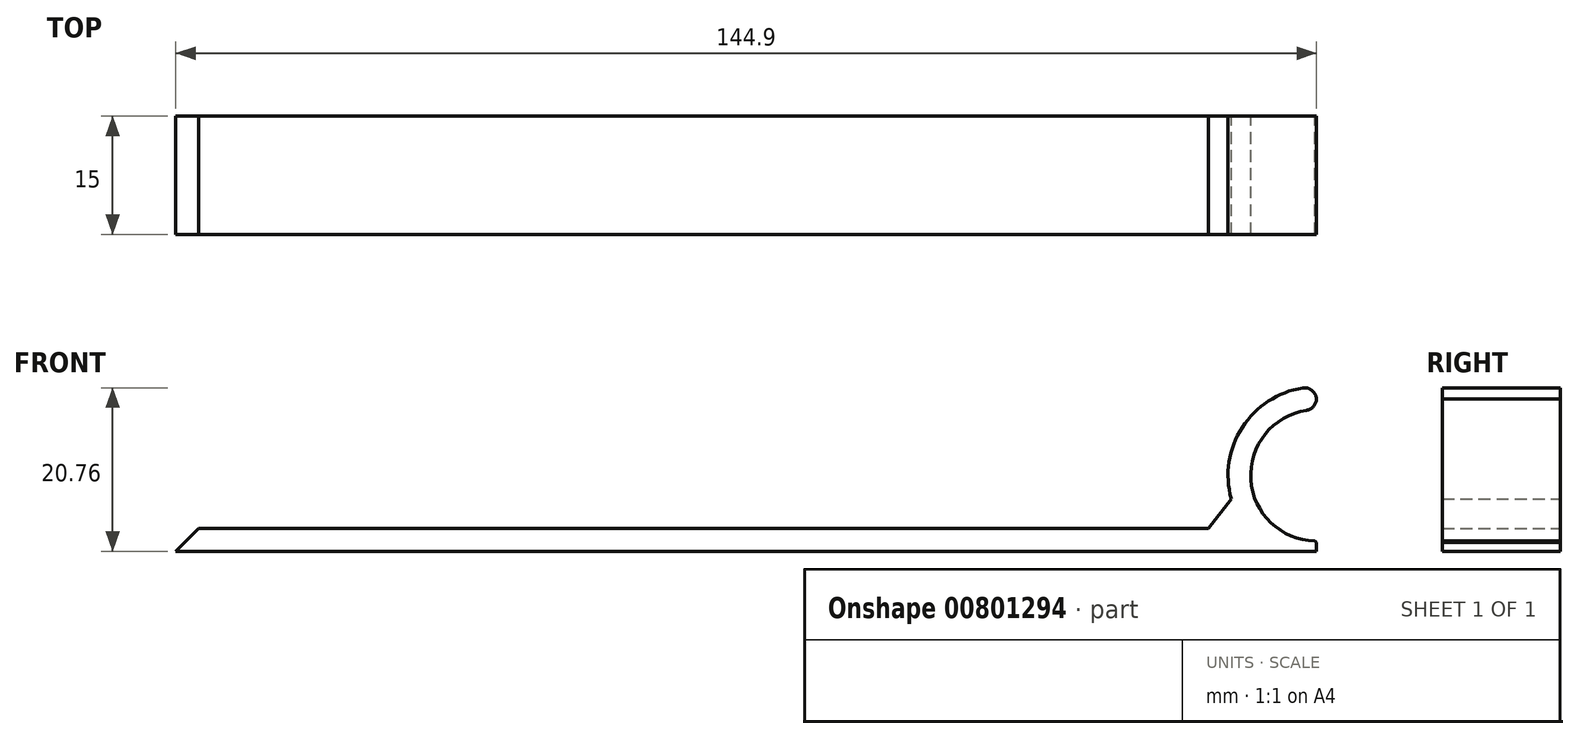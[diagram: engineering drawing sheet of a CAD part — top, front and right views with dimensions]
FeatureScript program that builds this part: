
annotation { "Feature Type Name" : "Feature", "Feature Type Description" : "" }
export const myFeature = defineFeature(function(context is Context, id is Id, definition is map)
    precondition{}
    {
        {
            var Q0;
            Q0=qCreatedBy(makeId("Front.planeOp"),FACE);
            var sketch = newSketch(context, id + "F0", { "sketchPlane" : qUnion([Q0])});
            skLineSegment(sketch, "E0.bottom", {"start": v(72.5, 1.58) * mm, "end": v(62.54, 1.58) * mm});
            skLineSegment(sketch, "E0.top", {"start": v(72.5, -1.58) * mm, "end": v(-72.5, -1.58) * mm});
            skLineSegment(sketch, "E0.left", {"start": v(72.5, 1.58) * mm, "end": v(72.5, -1.58) * mm});
            skLineSegment(sketch, "E0.right", {"start": v(-72.5, 0) * mm, "end": v(-72.5, -1.58) * mm});
            skPoint(sketch, "E0.middle", {"position": v(0, 0) * mm});
            skLineSegment(sketch, "E1", {"start": v(72.5, -1.58) * mm, "end": v(72.5, 6.77) * mm, "construction": true});
            skCircle(sketch, "E2", {"center": v(72.5, 6.77) * mm, "radius": 8.35 * mm});
            skCircle(sketch, "E3", {"center": v(72.5, 6.77) * mm, "radius": 11.23 * mm});
            skLineSegment(sketch, "E4", {"start": v(72.5, 15.12) * mm, "end": v(72.5, 18) * mm});
            skLineSegment(sketch, "E5.bottom", {"start": v(-72.5, -1.58) * mm, "end": v(72.5, -1.58) * mm});
            skLineSegment(sketch, "E5.top", {"start": v(-72.5, -2.88) * mm, "end": v(72.5, -2.88) * mm});
            skLineSegment(sketch, "E5.left", {"start": v(-72.5, -1.58) * mm, "end": v(-72.5, -2.88) * mm});
            skLineSegment(sketch, "E5.right", {"start": v(72.5, -1.58) * mm, "end": v(72.5, -2.88) * mm});
            skLineSegment(sketch, "E6.top", {"start": v(-72.5, 0) * mm, "end": v(72.5, 0) * mm});
            skLineSegment(sketch, "E6.left", {"start": v(-72.5, -1.58) * mm, "end": v(-72.5, 0) * mm});
            skLineSegment(sketch, "E6.right", {"start": v(72.5, -1.58) * mm, "end": v(72.5, 0) * mm});
            skPoint(sketch, "E7.orphan", {"position": v(-72.5, 1.58) * mm});
            skSolve(sketch);
        }
        {
            var Q0;
            {var subQ0=sQuery(id+"F0.wireOp",EDGE,"E0.right");Q0=makeQuery(id+"F0.imprint","IMPRINT",FACE,{"disambiguationData":[TD([[makeQuery(id+"F0.imprint","IMPRINT",EDGE,{"derivedFrom":subQ0}),1.0]])]});}
            var Q1;
            {var subQ0=sQuery(id+"F0.wireOp",EDGE,"E0.left");var subQ1=sQuery(id+"F0.wireOp",EDGE,"E0.top");var subQ2=makeQuery(id+"F0.imprint","INTERSECT",VERTEX,{"derivedFrom":[subQ1,subQ0]});Q1=makeQuery(id+"F0.imprint","IMPRINT",FACE,{"disambiguationData":[TD([[makeQuery(id+"F0.imprint","IMPRINT",EDGE,{"disambiguationData":[TD([[subQ2,-1.0]])],"derivedFrom":subQ1}),-1.0]])]});}
            var Q2;
            {var subQ5=sQuery(id+"F0.wireOp",EDGE,"urySj7C3-RO8u-xJS9-4BbJ-Gt5VhAMPYNj5");Q2=makeQuery(id+"F0.imprint","IMPRINT",FACE,{"disambiguationData":[TD([[makeQuery(id+"F0.imprint","IMPRINT",EDGE,{"derivedFrom":subQ5}),1.0]])]});}
            var Q3;
            {var subQ5=sQuery(id+"F0.wireOp",EDGE,"E4");Q3=makeQuery(id+"F0.imprint","IMPRINT",FACE,{"disambiguationData":[TD([[makeQuery(id+"F0.imprint","IMPRINT",EDGE,{"derivedFrom":subQ5}),1.0]])]});}
            var Q4;
            {var subQ5=sQuery(id+"F0.wireOp",EDGE,"E5.left");Q4=makeQuery(id+"F0.imprint","IMPRINT",FACE,{"disambiguationData":[TD([[makeQuery(id+"F0.imprint","IMPRINT",EDGE,{"derivedFrom":subQ5}),1.0]])]});}
            var Q5;
            {var subQ0=sQuery(id+"F0.wireOp",EDGE,"E3");var subQ1=sQuery(id+"F0.wireOp",EDGE,"E0.bottom");var subQ2=makeQuery(id+"F0.imprint","INTERSECT",VERTEX,{"derivedFrom":[subQ1,subQ0]});Q5=makeQuery(id+"F0.imprint","IMPRINT",FACE,{"disambiguationData":[TD([[makeQuery(id+"F0.imprint","IMPRINT",EDGE,{"disambiguationData":[TD([[subQ2,1.0]])],"derivedFrom":subQ1}),1.0]])]});}
            var Q6;
            {var subQ5=sQuery(id+"F0.wireOp",EDGE,"E5.right");Q6=makeQuery(id+"F0.imprint","IMPRINT",FACE,{"disambiguationData":[TD([[makeQuery(id+"F0.imprint","IMPRINT",EDGE,{"derivedFrom":subQ5}),-1.0]])]});}
            var Q7;
            {var subQ3=sQuery(id+"F0.wireOp",EDGE,"E6.top");var subQ5=sQuery(id+"F0.wireOp",EDGE,"E3");var subQ6=makeQuery(id+"F0.imprint","INTERSECT",VERTEX,{"derivedFrom":[subQ5,subQ3]});Q7=makeQuery(id+"F0.imprint","IMPRINT",FACE,{"disambiguationData":[TD([[makeQuery(id+"F0.imprint","IMPRINT",EDGE,{"disambiguationData":[TD([[subQ6,-1.0]])],"derivedFrom":subQ5}),1.0]])]});}
            var Q8;
            {var subQ5=sQuery(id+"F0.wireOp",EDGE,"E6.left");Q8=makeQuery(id+"F0.imprint","IMPRINT",FACE,{"disambiguationData":[TD([[makeQuery(id+"F0.imprint","IMPRINT",EDGE,{"derivedFrom":subQ5}),-1.0]])]});}
            extrude(context, id + "F1", {"entities" : qUnion([Q0, Q1, Q2, Q3, Q4, Q5, Q6, Q7, Q8]), "depth" : 15 * mm, "offsetDistance" : 25 * mm});
        }
        {
            var Q0;
            Q0=makeQuery(id+"F1.opExtrude","SWEPT_EDGE",EDGE,{"disambiguationData":[OSD([sQuery(id+"F0.wireOp",EDGE,"E0.top"),sQuery(id+"F0.wireOp",EDGE,"E0.left"),sQuery(id+"F0.wireOp",EDGE,"E2")])]});
            var Q1;
            Q1=makeQuery(id+"F1.opExtrude","SWEPT_EDGE",EDGE,{"disambiguationData":[OSD([sQuery(id+"F0.wireOp",EDGE,"E2"),sQuery(id+"F0.wireOp",EDGE,"E5.right"),sQuery(id+"F0.wireOp",EDGE,"E5.bottom"),sQuery(id+"F0.wireOp",EDGE,"E6.right")])]});
            chamfer(context, id + "F2", {"entities" : qUnion([Q0, Q1]), "width" : 0.2 * mm, "tangentPropagation" : true});
        }
        {
            var Q0;
            Q0=makeQuery(id+"F1.opExtrude","SWEPT_EDGE",EDGE,{"disambiguationData":[OSD([sQuery(id+"F0.wireOp",EDGE,"E0.bottom"),sQuery(id+"F0.wireOp",EDGE,"E0.right")])]});
            var Q1;
            Q1=makeQuery(id+"F1.opExtrude","SWEPT_EDGE",EDGE,{"disambiguationData":[OSD([sQuery(id+"F0.wireOp",EDGE,"E6.top"),sQuery(id+"F0.wireOp",EDGE,"E6.left")])]});
            chamfer(context, id + "F3", {"entities" : qUnion([Q0, Q1]), "chamferType" : ChamferType.OFFSET_ANGLE, "width" : 2.98 * mm, "oppositeDirection" : false, "angle" : 45 * degree, "tangentPropagation" : true});
        }
        {
            var Q0;
            Q0=makeQuery(id+"F1.opExtrude","SWEPT_EDGE",EDGE,{"disambiguationData":[OSD([sQuery(id+"F0.wireOp",EDGE,"E2"),sQuery(id+"F0.wireOp",EDGE,"E4")])]});
            var Q1;
            Q1=makeQuery(id+"F1.opExtrude","SWEPT_EDGE",EDGE,{"disambiguationData":[OSD([sQuery(id+"F0.wireOp",EDGE,"E3"),sQuery(id+"F0.wireOp",EDGE,"E4")])]});
            fillet(context, id + "F4", {"entities" : qUnion([Q0, Q1]), "radius" : 1.5 * mm, "tangentPropagation" : true, "allowEdgeOverflow" : false});
        }
    });
